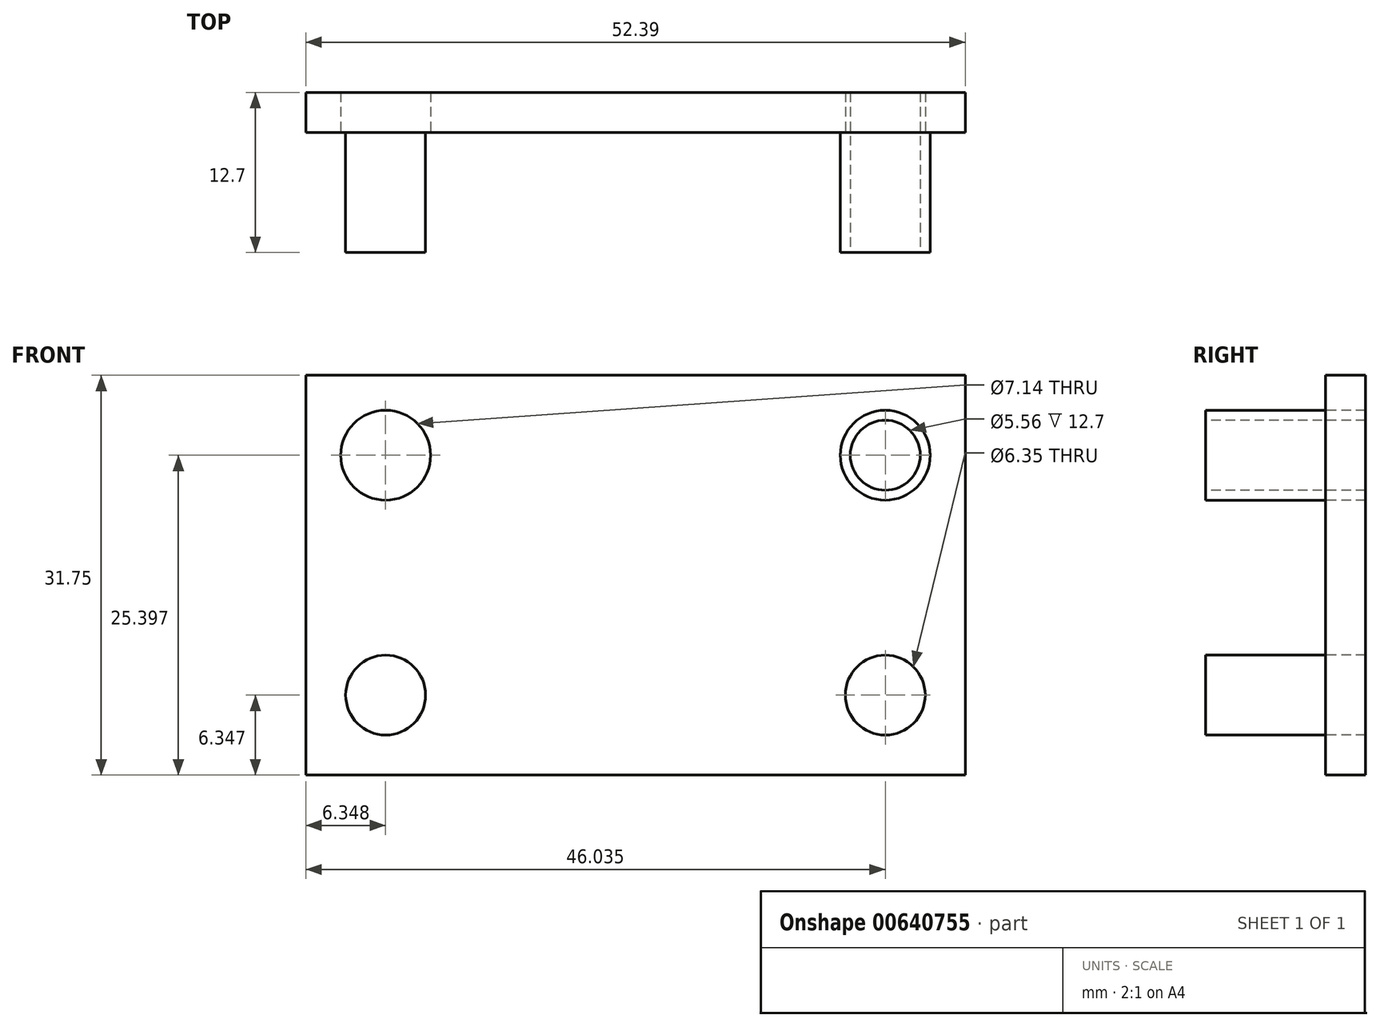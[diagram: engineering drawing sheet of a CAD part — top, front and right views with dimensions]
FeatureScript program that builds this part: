
annotation { "Feature Type Name" : "Feature", "Feature Type Description" : "" }
export const myFeature = defineFeature(function(context is Context, id is Id, definition is map)
    precondition{}
    {
        {
            var Q0;
            Q0=qCreatedBy(makeId("Front.planeOp"),FACE);
            var sketch = newSketch(context, id + "F0", { "sketchPlane" : qUnion([Q0])});
            skLineSegment(sketch, "E0.bottom", {"start": v(-24.21, 7.17) * mm, "end": v(28.18, 7.17) * mm});
            skLineSegment(sketch, "E0.top", {"start": v(-24.21, -24.58) * mm, "end": v(28.18, -24.58) * mm});
            skLineSegment(sketch, "E0.left", {"start": v(-24.21, 7.17) * mm, "end": v(-24.21, -24.58) * mm});
            skLineSegment(sketch, "E0.right", {"start": v(28.18, 7.17) * mm, "end": v(28.18, -24.58) * mm});
            skSolve(sketch);
        }
        {
            var Q0;
            Q0=makeQuery(id+"F0.imprint","IMPRINT",FACE,{"disambiguationData":[TD([[makeQuery(id+"F0.imprint","IMPRINT",EDGE,{"derivedFrom":sQuery(id+"F0.wireOp",EDGE,"E0.bottom")}),-1.0]])]});
            extrude(context, id + "F1", {"entities" : qUnion([Q0]), "depth" : 3.17 * mm, "offsetDistance" : 25.4 * mm});
        }
        {
            var Q0;
            Q0=makeQuery(id+"F1.opExtrude","CAP_FACE",FACE,{"disambiguationData":[OSD([sQuery(id+"F0.wireOp",EDGE,"E0.bottom"),sQuery(id+"F0.wireOp",EDGE,"E0.top"),sQuery(id+"F0.wireOp",EDGE,"E0.left"),sQuery(id+"F0.wireOp",EDGE,"E0.right")])],"isStart":false});
            var sketch = newSketch(context, id + "F2", { "sketchPlane" : qUnion([Q0])});
            skLineSegment(sketch, "E1", {"start": v(-24.21, 7.17) * mm, "end": v(-24.21, 0.82) * mm});
            skLineSegment(sketch, "E2", {"start": v(-24.21, 0.82) * mm, "end": v(-17.86, 0.82) * mm});
            skCircle(sketch, "E3", {"center": v(-17.86, 0.82) * mm, "radius": 3.57 * mm});
            skSolve(sketch);
        }
        {
            var Q0;
            Q0=makeQuery(id+"F2.imprint","IMPRINT",FACE,{"disambiguationData":[TD([[makeQuery(id+"F2.imprint","IMPRINT",EDGE,{"derivedFrom":sQuery(id+"F2.wireOp",EDGE,"E3")}),1.0]])]});
            extrude(context, id + "F3", {"entities" : qUnion([Q0]), "operationType" : NewBodyOperationType.REMOVE, "endBound" : BoundingType.THROUGH_ALL, "oppositeDirection" : true, "depth" : 25.4 * mm});
        }
        {
            var Q0;
            Q0=makeQuery(id+"F1.opExtrude","CAP_FACE",FACE,{"disambiguationData":[OSD([sQuery(id+"F0.wireOp",EDGE,"E0.bottom"),sQuery(id+"F0.wireOp",EDGE,"E0.top"),sQuery(id+"F0.wireOp",EDGE,"E0.left"),sQuery(id+"F0.wireOp",EDGE,"E0.right")])],"isStart":false});
            var sketch = newSketch(context, id + "F4", { "sketchPlane" : qUnion([Q0])});
            skLineSegment(sketch, "E4", {"start": v(28.18, 7.17) * mm, "end": v(28.18, 0.82) * mm});
            skLineSegment(sketch, "E5", {"start": v(28.18, 0.82) * mm, "end": v(21.83, 0.82) * mm});
            skCircle(sketch, "E6", {"center": v(21.83, 0.82) * mm, "radius": 3.57 * mm});
            skSolve(sketch);
        }
        {
            var Q0;
            Q0=makeQuery(id+"F4.imprint","IMPRINT",FACE,{"disambiguationData":[TD([[makeQuery(id+"F4.imprint","IMPRINT",EDGE,{"derivedFrom":sQuery(id+"F4.wireOp",EDGE,"E6")}),1.0]])]});
            extrude(context, id + "F5", {"entities" : qUnion([Q0]), "operationType" : NewBodyOperationType.ADD, "depth" : 9.52 * mm});
        }
        {
            var Q0;
            Q0=makeQuery(id+"F5.opExtrude","CAP_FACE",FACE,{"disambiguationData":[OSD([sQuery(id+"F4.wireOp",EDGE,"E6")])],"isStart":false});
            var sketch = newSketch(context, id + "F6", { "sketchPlane" : qUnion([Q0])});
            skCircle(sketch, "E7", {"center": v(21.83, 0.82) * mm, "radius": 2.78 * mm});
            skSolve(sketch);
        }
        {
            var Q0;
            Q0=makeQuery(id+"F6.imprint","IMPRINT",FACE,{"disambiguationData":[TD([[makeQuery(id+"F6.imprint","IMPRINT",EDGE,{"derivedFrom":sQuery(id+"F6.wireOp",EDGE,"E7")}),1.0]])]});
            extrude(context, id + "F7", {"entities" : qUnion([Q0]), "operationType" : NewBodyOperationType.REMOVE, "endBound" : BoundingType.THROUGH_ALL, "oppositeDirection" : true, "depth" : 25.4 * mm});
        }
        {
            var Q0;
            Q0=makeQuery(id+"F1.opExtrude","CAP_FACE",FACE,{"disambiguationData":[OSD([sQuery(id+"F0.wireOp",EDGE,"E0.bottom"),sQuery(id+"F0.wireOp",EDGE,"E0.top"),sQuery(id+"F0.wireOp",EDGE,"E0.left"),sQuery(id+"F0.wireOp",EDGE,"E0.right")])],"isStart":false});
            var sketch = newSketch(context, id + "F8", { "sketchPlane" : qUnion([Q0])});
            skLineSegment(sketch, "E8", {"start": v(-24.21, -24.58) * mm, "end": v(-24.21, -18.23) * mm});
            skLineSegment(sketch, "E9", {"start": v(-24.21, -18.23) * mm, "end": v(-17.86, -18.23) * mm});
            skCircle(sketch, "E10", {"center": v(-17.86, -18.23) * mm, "radius": 3.18 * mm});
            skSolve(sketch);
        }
        {
            var Q0;
            Q0=makeQuery(id+"F8.imprint","IMPRINT",FACE,{"disambiguationData":[TD([[makeQuery(id+"F8.imprint","IMPRINT",EDGE,{"derivedFrom":sQuery(id+"F8.wireOp",EDGE,"E10")}),1.0]])]});
            extrude(context, id + "F9", {"entities" : qUnion([Q0]), "operationType" : NewBodyOperationType.ADD, "depth" : 9.52 * mm});
        }
        {
            var Q0;
            Q0=makeQuery(id+"F1.opExtrude","CAP_FACE",FACE,{"disambiguationData":[OSD([sQuery(id+"F0.wireOp",EDGE,"E0.bottom"),sQuery(id+"F0.wireOp",EDGE,"E0.top"),sQuery(id+"F0.wireOp",EDGE,"E0.left"),sQuery(id+"F0.wireOp",EDGE,"E0.right")])],"isStart":false});
            var sketch = newSketch(context, id + "F10", { "sketchPlane" : qUnion([Q0])});
            skLineSegment(sketch, "E11", {"start": v(28.18, -24.58) * mm, "end": v(28.18, -18.23) * mm});
            skLineSegment(sketch, "E12", {"start": v(28.18, -18.23) * mm, "end": v(21.83, -18.23) * mm});
            skCircle(sketch, "E13", {"center": v(21.83, -18.23) * mm, "radius": 3.18 * mm});
            skSolve(sketch);
        }
        {
            var Q0;
            Q0=makeQuery(id+"F10.imprint","IMPRINT",FACE,{"disambiguationData":[TD([[makeQuery(id+"F10.imprint","IMPRINT",EDGE,{"derivedFrom":sQuery(id+"F10.wireOp",EDGE,"E13")}),1.0]])]});
            extrude(context, id + "F11", {"entities" : qUnion([Q0]), "operationType" : NewBodyOperationType.REMOVE, "endBound" : BoundingType.THROUGH_ALL, "oppositeDirection" : true, "depth" : 25.4 * mm});
        }
    });
